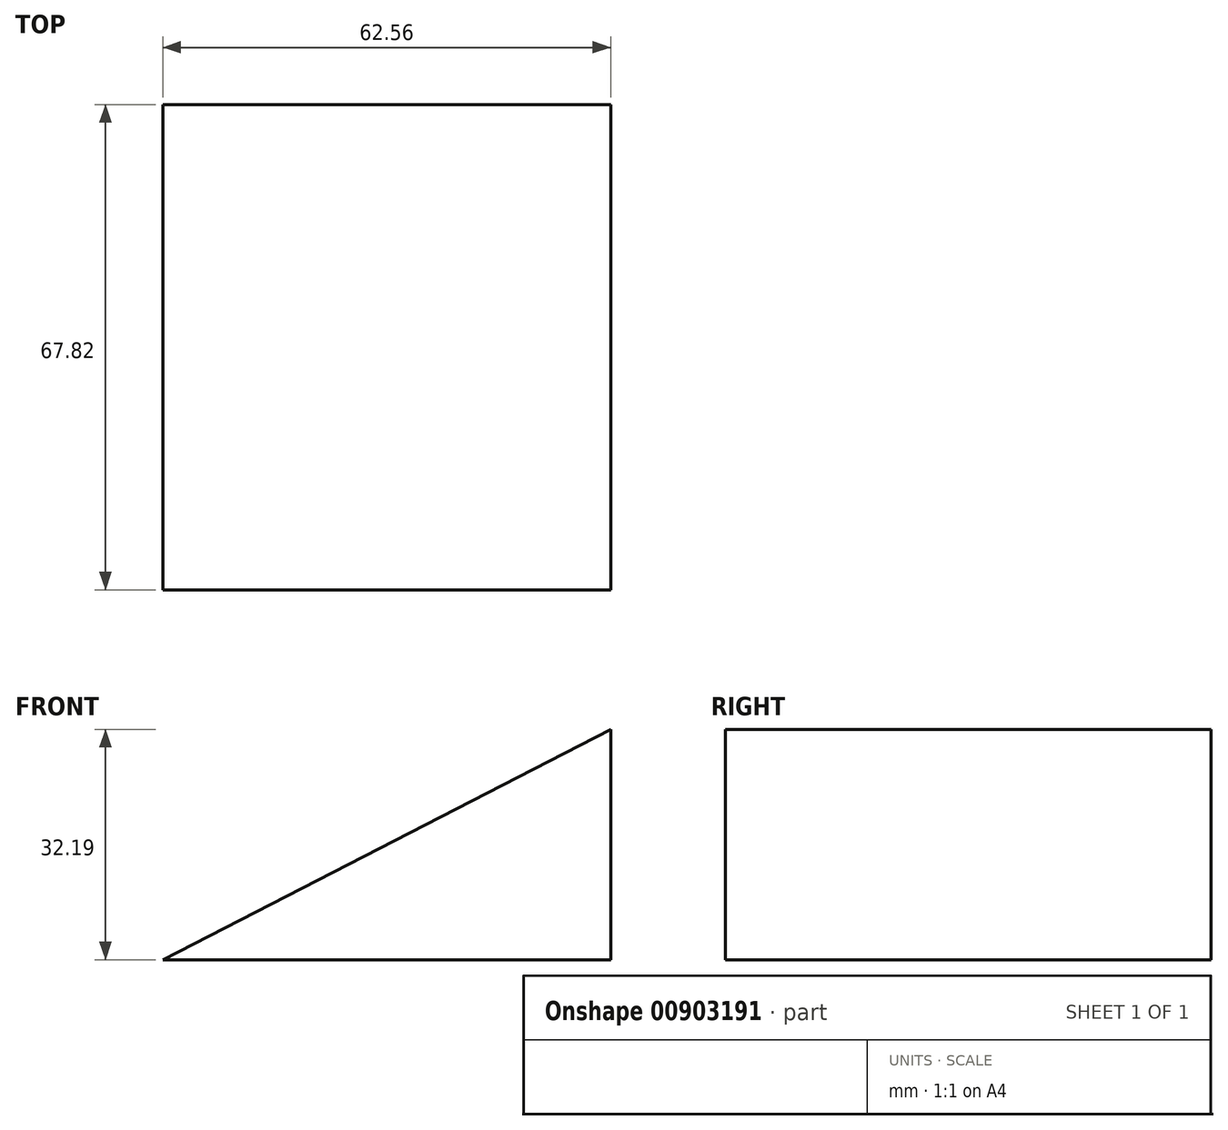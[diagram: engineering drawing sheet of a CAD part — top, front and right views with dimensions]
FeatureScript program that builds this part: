
annotation { "Feature Type Name" : "Feature", "Feature Type Description" : "" }
export const myFeature = defineFeature(function(context is Context, id is Id, definition is map)
    precondition{}
    {
        {
            var Q0;
            Q0=qCreatedBy(makeId("Front.planeOp"),FACE);
            var sketch = newSketch(context, id + "F0", { "sketchPlane" : qUnion([Q0])});
            skLineSegment(sketch, "E0", {"start": v(-27.82, -14.89) * mm, "end": v(34.74, -14.89) * mm});
            skLineSegment(sketch, "E1", {"start": v(34.74, -14.89) * mm, "end": v(34.74, 17.3) * mm});
            skLineSegment(sketch, "E2", {"start": v(34.74, 17.3) * mm, "end": v(-27.82, -14.89) * mm});
            skSolve(sketch);
        }
        {
            var Q0;
            Q0=makeQuery(id+"F0.imprint","IMPRINT",FACE,{"disambiguationData":[TD([[makeQuery(id+"F0.imprint","IMPRINT",EDGE,{"derivedFrom":sQuery(id+"F0.wireOp",EDGE,"E0")}),1.0]])]});
            extrude(context, id + "F1", {"entities" : qUnion([Q0]), "depth" : 67.82 * mm, "offsetDistance" : 25.4 * mm});
        }
    });
